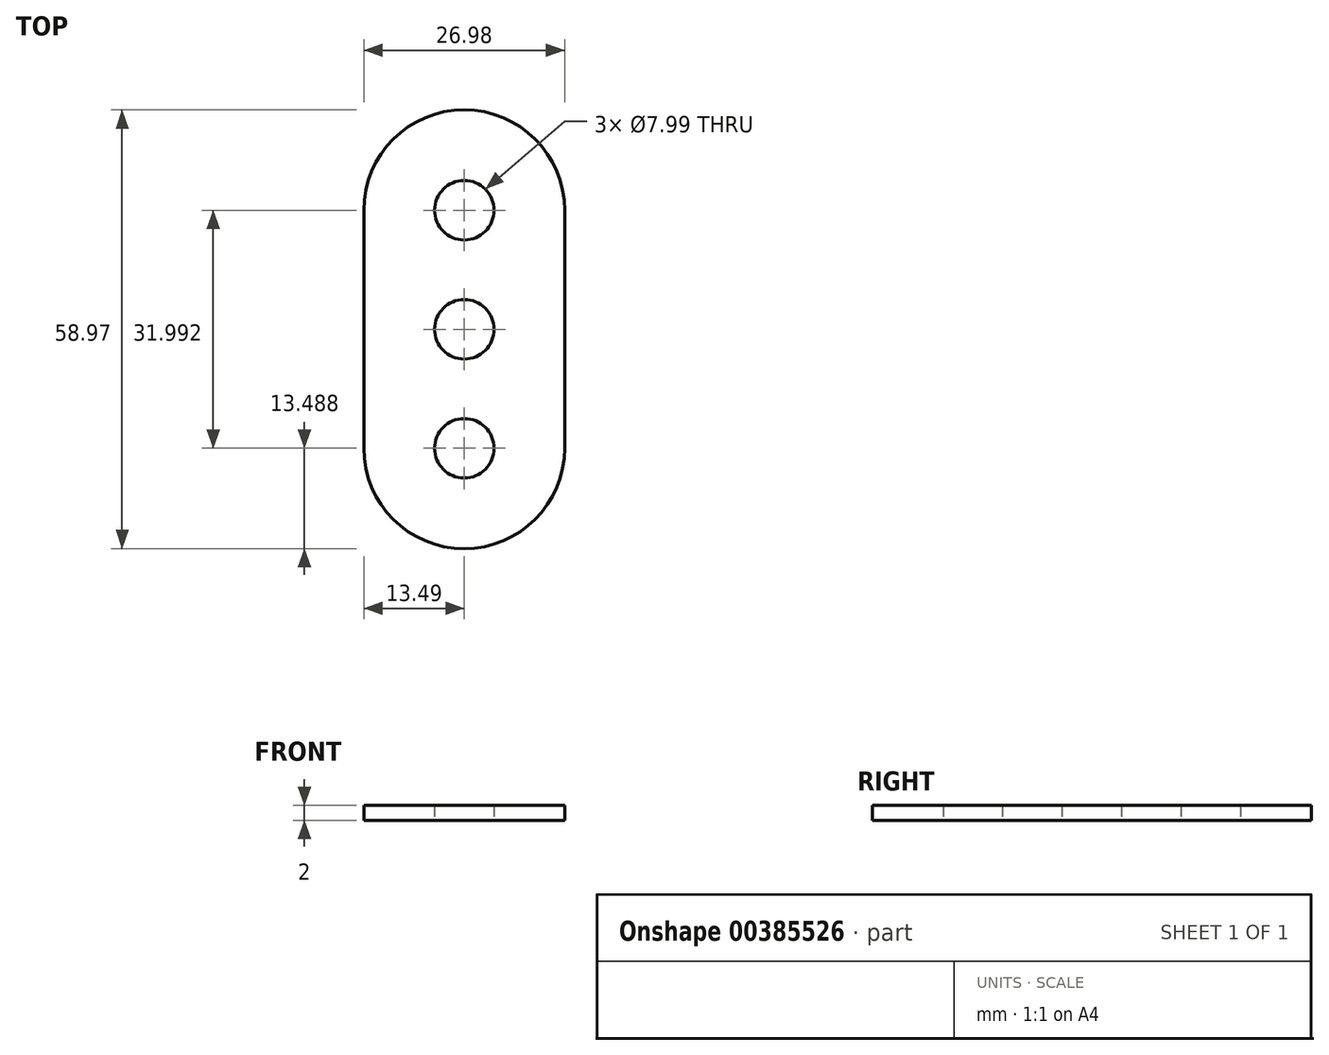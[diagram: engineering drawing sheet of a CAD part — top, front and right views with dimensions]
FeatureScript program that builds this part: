
annotation { "Feature Type Name" : "Feature", "Feature Type Description" : "" }
export const myFeature = defineFeature(function(context is Context, id is Id, definition is map)
    precondition{}
    {
        {
            var Q0;
            Q0=qCreatedBy(makeId("Top.planeOp"),FACE);
            var sketch = newSketch(context, id + "F0", { "sketchPlane" : qUnion([Q0])});
            skLineSegment(sketch, "E0.bottom", {"start": v(13.5, -29.49) * mm, "end": v(-13.49, -29.49) * mm});
            skLineSegment(sketch, "E0.top", {"start": v(13.49, 29.49) * mm, "end": v(-13.5, 29.49) * mm});
            skLineSegment(sketch, "E0.left", {"start": v(13.5, -29.49) * mm, "end": v(13.49, 29.49) * mm});
            skLineSegment(sketch, "E0.right", {"start": v(-13.49, -29.49) * mm, "end": v(-13.5, 29.49) * mm});
            skPoint(sketch, "E0.middle", {"position": v(0, 0) * mm});
            skCircle(sketch, "E1", {"center": v(0, 16) * mm, "radius": 13.49 * mm});
            skCircle(sketch, "E2", {"center": v(0, -16) * mm, "radius": 13.5 * mm});
            skCircle(sketch, "E3", {"center": v(0, -16) * mm, "radius": 4 * mm});
            skCircle(sketch, "E4", {"center": v(0, 16) * mm, "radius": 4 * mm});
            skLineSegment(sketch, "E5", {"start": v(0, -16) * mm, "end": v(0, -8) * mm, "construction": true});
            skLineSegment(sketch, "E6", {"start": v(0, -16) * mm, "end": v(0, -24) * mm, "construction": true});
            skLineSegment(sketch, "E7", {"start": v(0, 16) * mm, "end": v(0, 24) * mm, "construction": true});
            skCircle(sketch, "E8", {"center": v(0, 0) * mm, "radius": 4 * mm});
            skSolve(sketch);
        }
        {
            var Q0;
            Q0 = qSketchRegion(id + "F0", true);
            extrude(context, id + "F1", {"entities" : qUnion([Q0]), "depth" : 2 * mm});
        }
        {
            var Q0;
            {var subQ0=sQuery(id+"F0.wireOp",EDGE,"E0.left");var subQ1=sQuery(id+"F0.wireOp",EDGE,"E0.top");var subQ2=makeQuery(id+"F0.imprint","INTERSECT",VERTEX,{"derivedFrom":[subQ1,subQ0]});Q0=makeQuery(id+"F0.imprint","IMPRINT",FACE,{"disambiguationData":[TD([[makeQuery(id+"F0.imprint","IMPRINT",EDGE,{"disambiguationData":[TD([[subQ2,-1.0]])],"derivedFrom":subQ1}),1.0]])]});}
            var Q1;
            {var subQ0=sQuery(id+"F0.wireOp",EDGE,"E0.right");var subQ1=sQuery(id+"F0.wireOp",EDGE,"E0.bottom");var subQ2=makeQuery(id+"F0.imprint","INTERSECT",VERTEX,{"derivedFrom":[subQ1,subQ0]});Q1=makeQuery(id+"F0.imprint","IMPRINT",FACE,{"disambiguationData":[TD([[makeQuery(id+"F0.imprint","IMPRINT",EDGE,{"disambiguationData":[TD([[subQ2,1.0]])],"derivedFrom":subQ1}),-1.0]])]});}
            var Q2;
            {var subQ0=sQuery(id+"F0.wireOp",EDGE,"E0.left");var subQ1=sQuery(id+"F0.wireOp",EDGE,"E0.bottom");var subQ2=makeQuery(id+"F0.imprint","INTERSECT",VERTEX,{"derivedFrom":[subQ1,subQ0]});Q2=makeQuery(id+"F0.imprint","IMPRINT",FACE,{"disambiguationData":[TD([[makeQuery(id+"F0.imprint","IMPRINT",EDGE,{"disambiguationData":[TD([[subQ2,-1.0]])],"derivedFrom":subQ1}),-1.0]])]});}
            var Q3;
            {var subQ0=sQuery(id+"F0.wireOp",EDGE,"E0.right");var subQ1=sQuery(id+"F0.wireOp",EDGE,"E0.top");var subQ2=makeQuery(id+"F0.imprint","INTERSECT",VERTEX,{"derivedFrom":[subQ1,subQ0]});Q3=makeQuery(id+"F0.imprint","IMPRINT",FACE,{"disambiguationData":[TD([[makeQuery(id+"F0.imprint","IMPRINT",EDGE,{"disambiguationData":[TD([[subQ2,1.0]])],"derivedFrom":subQ1}),1.0]])]});}
            extrude(context, id + "F2", {"entities" : qUnion([Q0, Q1, Q2, Q3]), "operationType" : NewBodyOperationType.REMOVE, "depth" : 25 * mm});
        }
    });
